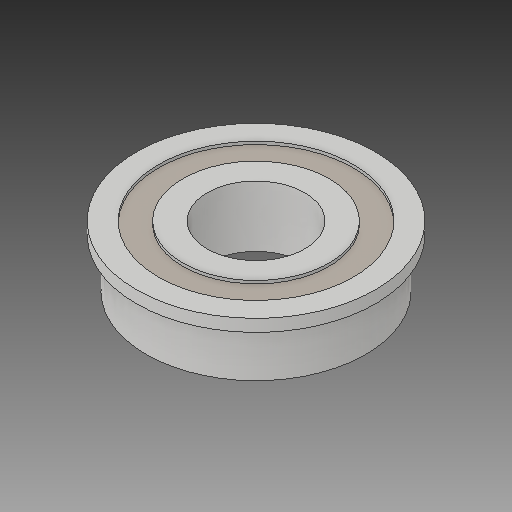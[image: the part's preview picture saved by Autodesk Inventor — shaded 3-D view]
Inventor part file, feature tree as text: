
AUTODESK INVENTOR PART (.ipt)
format: ipt  version: 2017 (Build 210142000, 142)  size: 138,240 bytes
history: native  units: in
note: dims shown in document units (in); Inventor stores cm internally (conversion verified against a paired STEP export)
features: revolve x1
ambient origin geometry x8: Origin, YZ Plane, XZ Plane, XY Plane, X Axis, Y Axis, Z Axis, Center Point
bodies: Solid1 (feature_tree)
feature tree (1):
  revolve  "Revolve1"  [1 undecoded]
note: 1 required parameter value undecoded (feature->parameter linkage not recoverable at this tier; creation-order binding heuristic only, values carry confidence <= 0.55)
